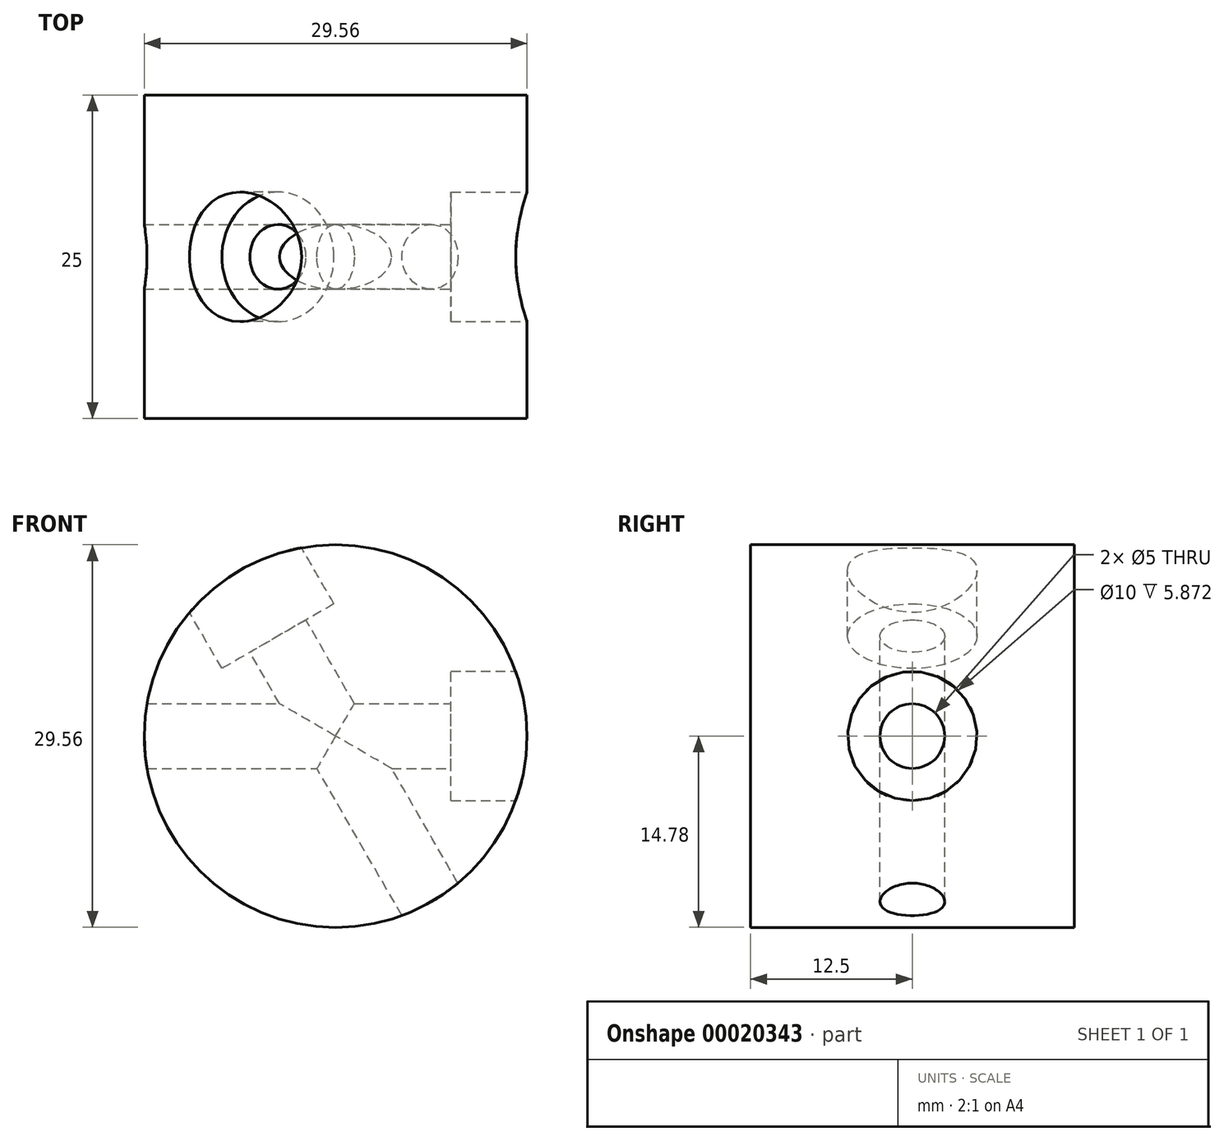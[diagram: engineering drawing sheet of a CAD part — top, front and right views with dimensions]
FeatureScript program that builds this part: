
annotation { "Feature Type Name" : "Feature", "Feature Type Description" : "" }
export const myFeature = defineFeature(function(context is Context, id is Id, definition is map)
    precondition{}
    {
        {
            var Q0;
            Q0=qCreatedBy(makeId("Front.planeOp"),FACE);
            var sketch = newSketch(context, id + "F0", { "sketchPlane" : qUnion([Q0])});
            skCircle(sketch, "E0", {"center": v(0, 0) * mm, "radius": 14.78 * mm});
            skPoint(sketch, "E1", {"position": v(14.78, 0) * mm});
            skSolve(sketch);
        }
        {
            var Q0;
            Q0=makeQuery(id+"F0.imprint","IMPRINT",FACE,{"disambiguationData":[TD([[makeQuery(id+"F0.imprint","IMPRINT",EDGE,{"derivedFrom":sQuery(id+"F0.wireOp",EDGE,"E0")}),1.0]])]});
            extrude(context, id + "F1", {"entities" : qUnion([Q0]), "endBound" : BoundingType.SYMMETRIC, "depth" : 25 * mm});
        }
        {
            var Q0;
            Q0=qCreatedBy(makeId("Right.planeOp"),FACE);
            var Q1;
            Q1=sQuery(id+"F0.wireOp",VERTEX,"E1");
            cPlane(context, id + "F2", {"entities" : qUnion([Q0, Q1]), "cplaneType" : CPlaneType.PLANE_POINT, "offset" : 150 * mm, "width" : 150 * mm, "height" : 150 * mm});
        }
        {
            var Q0;
            Q0=qCreatedBy(id+"F2.planeOp",FACE);
            var sketch = newSketch(context, id + "F3", { "sketchPlane" : qUnion([Q0])});
            skPoint(sketch, "E2", {"position": v(0, 0) * mm});
            skSolve(sketch);
        }
        {
            var Q0;
            Q0=qCreatedBy(makeId("Front.planeOp"),FACE);
            var sketch = newSketch(context, id + "F4", { "sketchPlane" : qUnion([Q0])});
            skLineSegment(sketch, "E3", {"start": v(0, 0) * mm, "end": v(0, 14.78) * mm, "construction": true});
            skLineSegment(sketch, "E4", {"start": v(0, 0) * mm, "end": v(-7.4, 12.8) * mm, "construction": true});
            skSolve(sketch);
        }
        {
            var Q0;
            Q0=sQuery(id+"F4.wireOp",EDGE,"E4");
            var Q1;
            Q1=sQuery(id+"F4.wireOp",VERTEX,"E4.end");
            cPlane(context, id + "F5", {"entities" : qUnion([Q0, Q1]), "cplaneType" : CPlaneType.LINE_POINT, "offset" : 150 * mm, "width" : 150 * mm, "height" : 150 * mm});
        }
        {
            var Q0;
            Q0=qCreatedBy(id+"F5.planeOp",FACE);
            var sketch = newSketch(context, id + "F6", { "sketchPlane" : qUnion([Q0])});
            skPoint(sketch, "E5", {"position": v(0, 0) * mm});
            skSolve(sketch);
        }
        {
            var Q0;
            Q0=sQuery(id+"F3.wireOp",VERTEX,"E2");
            var Q1;
            Q1=sQuery(id+"F6.wireOp",VERTEX,"E5");
            var Q2;
            Q2=makeQuery(id+"F1.opExtrude","SWEPT_BODY",BODY,{"disambiguationData":[OSD([sQuery(id+"F0.wireOp",EDGE,"E0")])]});
            hole(context, id + "F7", {"style" : HoleStyle.C_BORE, "holeDiameter" : 5 * mm, "cBoreDiameter" : 10 * mm, "cBoreDepth" : 5 * mm, "endStyle" : HoleEndStyle.THROUGH, "locations" : qUnion([Q0, Q1]), "scope" : qUnion([Q2])});
        }
    });
